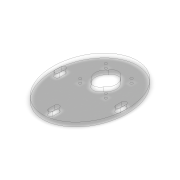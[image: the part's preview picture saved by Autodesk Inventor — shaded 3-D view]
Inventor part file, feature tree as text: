
AUTODESK INVENTOR PART (.ipt)
format: ipt  version: 2020 (Build 240168000, 168)  size: 190,464 bytes
history: native  units: in
note: dims shown in document units (in); Inventor stores cm internally (conversion verified against a paired STEP export)
features: extrude x1
ambient origin geometry x8: Origin, YZ Plane, XZ Plane, XY Plane, X Axis, Y Axis, Z Axis, Center Point
bodies: Body1 (feature_tree)
feature tree (1):
  extrude  "Extrusion4"  Depth=1.2205in
